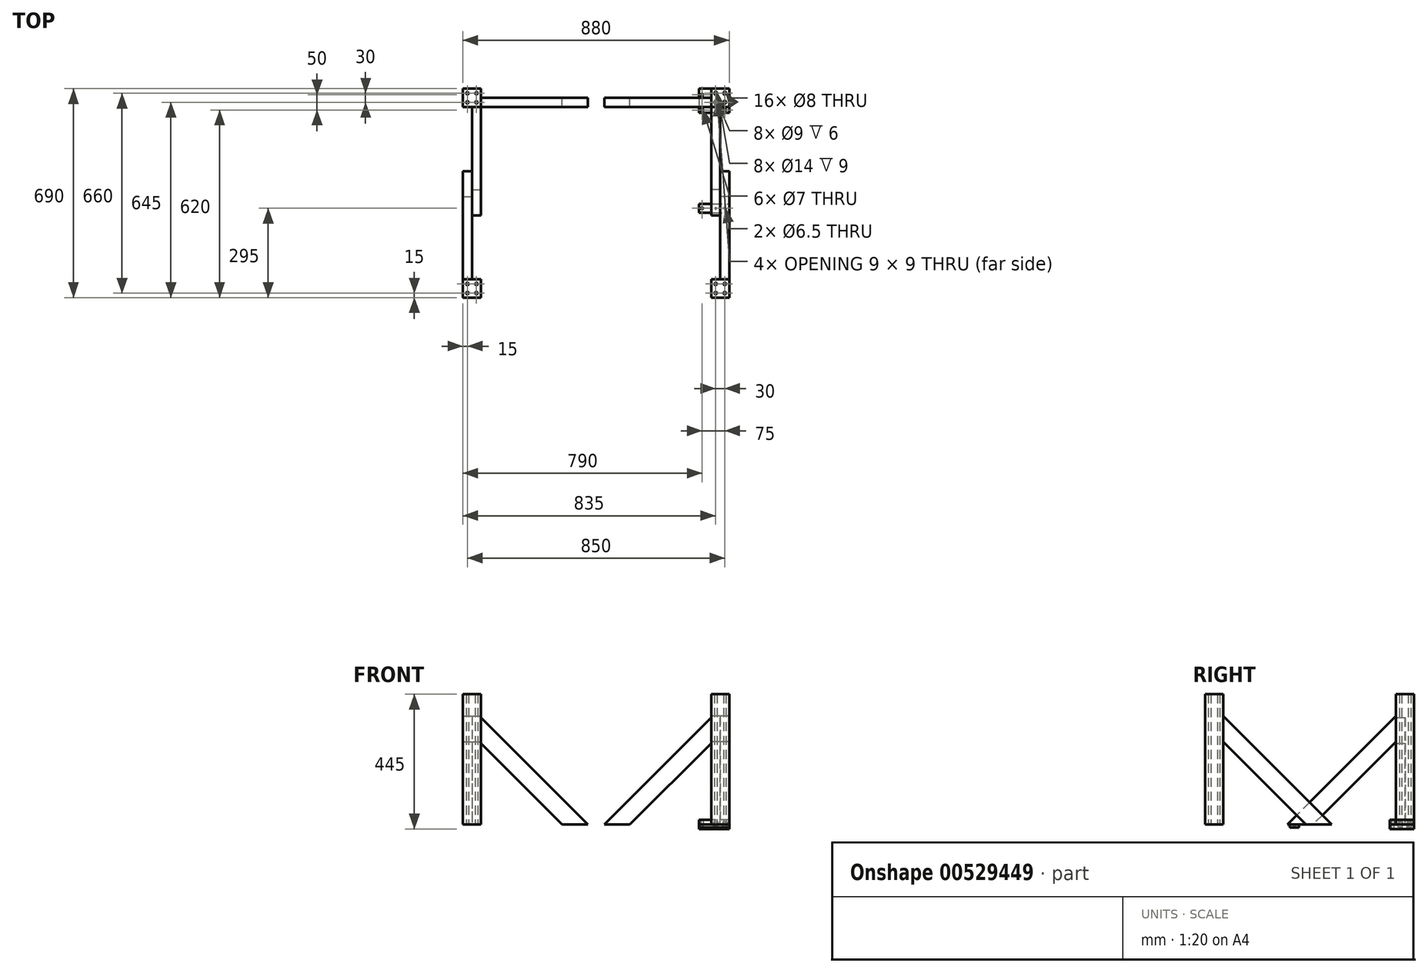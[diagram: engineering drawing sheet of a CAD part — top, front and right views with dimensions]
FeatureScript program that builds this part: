
annotation { "Feature Type Name" : "Feature", "Feature Type Description" : "" }
export const myFeature = defineFeature(function(context is Context, id is Id, definition is map)
    precondition{}
    {
        {
            var Q0;
            Q0=qCreatedBy(makeId("Top.planeOp"),FACE);
            var sketch = newSketch(context, id + "F0", { "sketchPlane" : qUnion([Q0])});
            skCircle(sketch, "E0", {"center": v(0, 0) * mm, "radius": 3 * mm, "construction": true});
            skCircle(sketch, "E1.0.1.0", {"center": v(0, 25) * mm, "radius": 3 * mm, "construction": true});
            skCircle(sketch, "E1.0.2.0", {"center": v(0, 50) * mm, "radius": 3 * mm, "construction": true});
            skCircle(sketch, "E1.0.3.0", {"center": v(0, 75) * mm, "radius": 3 * mm, "construction": true});
            skCircle(sketch, "E1.0.4.0", {"center": v(0, 100) * mm, "radius": 3 * mm, "construction": true});
            skCircle(sketch, "E1.1.0.0", {"center": v(25, 0) * mm, "radius": 3 * mm, "construction": true});
            skCircle(sketch, "E1.1.1.0", {"center": v(25, 25) * mm, "radius": 3 * mm, "construction": true});
            skCircle(sketch, "E1.1.2.0", {"center": v(25, 50) * mm, "radius": 3 * mm, "construction": true});
            skCircle(sketch, "E1.1.3.0", {"center": v(25, 75) * mm, "radius": 3 * mm, "construction": true});
            skCircle(sketch, "E1.1.4.0", {"center": v(25, 100) * mm, "radius": 3 * mm, "construction": true});
            skCircle(sketch, "E1.2.0.0", {"center": v(50, 0) * mm, "radius": 3 * mm, "construction": true});
            skCircle(sketch, "E1.2.1.0", {"center": v(50, 25) * mm, "radius": 3 * mm, "construction": true});
            skCircle(sketch, "E1.2.2.0", {"center": v(50, 50) * mm, "radius": 3 * mm, "construction": true});
            skCircle(sketch, "E1.2.3.0", {"center": v(50, 75) * mm, "radius": 3 * mm, "construction": true});
            skCircle(sketch, "E1.2.4.0", {"center": v(50, 100) * mm, "radius": 3 * mm, "construction": true});
            skCircle(sketch, "E1.3.0.0", {"center": v(75, 0) * mm, "radius": 3 * mm, "construction": true});
            skCircle(sketch, "E1.3.1.0", {"center": v(75, 25) * mm, "radius": 3 * mm, "construction": true});
            skCircle(sketch, "E1.3.2.0", {"center": v(75, 50) * mm, "radius": 3 * mm, "construction": true});
            skCircle(sketch, "E1.3.3.0", {"center": v(75, 75) * mm, "radius": 3 * mm, "construction": true});
            skCircle(sketch, "E1.3.4.0", {"center": v(75, 100) * mm, "radius": 3 * mm, "construction": true});
            skCircle(sketch, "E1.4.0.0", {"center": v(100, 0) * mm, "radius": 3 * mm, "construction": true});
            skCircle(sketch, "E1.4.1.0", {"center": v(100, 25) * mm, "radius": 3 * mm, "construction": true});
            skCircle(sketch, "E1.4.2.0", {"center": v(100, 50) * mm, "radius": 3 * mm, "construction": true});
            skCircle(sketch, "E1.4.3.0", {"center": v(100, 75) * mm, "radius": 3 * mm, "construction": true});
            skCircle(sketch, "E1.4.4.0", {"center": v(100, 100) * mm, "radius": 3 * mm, "construction": true});
            skLineSegment(sketch, "E1.direction1", {"start": v(0, 0) * mm, "end": v(25, 0) * mm, "construction": true});
            skLineSegment(sketch, "E1.direction2", {"start": v(0, 0) * mm, "end": v(0, 25) * mm, "construction": true});
            skCircle(sketch, "E2.0.1.0", {"center": v(0, -25) * mm, "radius": 3 * mm, "construction": true});
            skCircle(sketch, "E2.0.2.0", {"center": v(0, -50) * mm, "radius": 3 * mm, "construction": true});
            skCircle(sketch, "E2.0.3.0", {"center": v(0, -75) * mm, "radius": 3 * mm, "construction": true});
            skCircle(sketch, "E2.0.4.0", {"center": v(0, -100) * mm, "radius": 3 * mm, "construction": true});
            skCircle(sketch, "E2.0.5.0", {"center": v(0, -125) * mm, "radius": 3 * mm, "construction": true});
            skCircle(sketch, "E2.0.6.0", {"center": v(0, -150) * mm, "radius": 3 * mm, "construction": true});
            skCircle(sketch, "E2.0.7.0", {"center": v(0, -175) * mm, "radius": 3 * mm, "construction": true});
            skCircle(sketch, "E2.0.8.0", {"center": v(0, -200) * mm, "radius": 3 * mm, "construction": true});
            skCircle(sketch, "E2.0.9.0", {"center": v(0, -225) * mm, "radius": 3 * mm, "construction": true});
            skCircle(sketch, "E2.0.10.0", {"center": v(0, -250) * mm, "radius": 3 * mm, "construction": true});
            skCircle(sketch, "E2.0.11.0", {"center": v(0, -275) * mm, "radius": 3 * mm, "construction": true});
            skCircle(sketch, "E2.0.12.0", {"center": v(0, -300) * mm, "radius": 3 * mm, "construction": true});
            skCircle(sketch, "E2.0.13.0", {"center": v(0, -325) * mm, "radius": 3 * mm, "construction": true});
            skCircle(sketch, "E2.0.14.0", {"center": v(0, -350) * mm, "radius": 3 * mm, "construction": true});
            skCircle(sketch, "E2.0.15.0", {"center": v(0, -375) * mm, "radius": 3 * mm, "construction": true});
            skCircle(sketch, "E2.0.16.0", {"center": v(0, -400) * mm, "radius": 3 * mm, "construction": true});
            skCircle(sketch, "E2.0.17.0", {"center": v(0, -425) * mm, "radius": 3 * mm, "construction": true});
            skCircle(sketch, "E2.0.18.0", {"center": v(0, -450) * mm, "radius": 3 * mm, "construction": true});
            skCircle(sketch, "E2.0.19.0", {"center": v(0, -475) * mm, "radius": 3 * mm, "construction": true});
            skCircle(sketch, "E2.1.1.0", {"center": v(25, -25) * mm, "radius": 3 * mm, "construction": true});
            skCircle(sketch, "E2.1.2.0", {"center": v(25, -50) * mm, "radius": 3 * mm, "construction": true});
            skCircle(sketch, "E2.1.3.0", {"center": v(25, -75) * mm, "radius": 3 * mm, "construction": true});
            skCircle(sketch, "E2.1.4.0", {"center": v(25, -100) * mm, "radius": 3 * mm, "construction": true});
            skCircle(sketch, "E2.1.5.0", {"center": v(25, -125) * mm, "radius": 3 * mm, "construction": true});
            skCircle(sketch, "E2.1.6.0", {"center": v(25, -150) * mm, "radius": 3 * mm, "construction": true});
            skCircle(sketch, "E2.1.7.0", {"center": v(25, -175) * mm, "radius": 3 * mm, "construction": true});
            skCircle(sketch, "E2.1.8.0", {"center": v(25, -200) * mm, "radius": 3 * mm, "construction": true});
            skCircle(sketch, "E2.1.9.0", {"center": v(25, -225) * mm, "radius": 3 * mm, "construction": true});
            skCircle(sketch, "E2.1.10.0", {"center": v(25, -250) * mm, "radius": 3 * mm, "construction": true});
            skCircle(sketch, "E2.1.11.0", {"center": v(25, -275) * mm, "radius": 3 * mm, "construction": true});
            skCircle(sketch, "E2.1.12.0", {"center": v(25, -300) * mm, "radius": 3 * mm, "construction": true});
            skCircle(sketch, "E2.1.13.0", {"center": v(25, -325) * mm, "radius": 3 * mm, "construction": true});
            skCircle(sketch, "E2.1.14.0", {"center": v(25, -350) * mm, "radius": 3 * mm, "construction": true});
            skCircle(sketch, "E2.1.15.0", {"center": v(25, -375) * mm, "radius": 3 * mm, "construction": true});
            skCircle(sketch, "E2.1.16.0", {"center": v(25, -400) * mm, "radius": 3 * mm, "construction": true});
            skCircle(sketch, "E2.1.17.0", {"center": v(25, -425) * mm, "radius": 3 * mm, "construction": true});
            skCircle(sketch, "E2.1.18.0", {"center": v(25, -450) * mm, "radius": 3 * mm, "construction": true});
            skCircle(sketch, "E2.1.19.0", {"center": v(25, -475) * mm, "radius": 3 * mm, "construction": true});
            skCircle(sketch, "E2.2.1.0", {"center": v(50, -25) * mm, "radius": 3 * mm, "construction": true});
            skCircle(sketch, "E2.2.2.0", {"center": v(50, -50) * mm, "radius": 3 * mm, "construction": true});
            skCircle(sketch, "E2.2.3.0", {"center": v(50, -75) * mm, "radius": 3 * mm, "construction": true});
            skCircle(sketch, "E2.2.4.0", {"center": v(50, -100) * mm, "radius": 3 * mm, "construction": true});
            skCircle(sketch, "E2.2.5.0", {"center": v(50, -125) * mm, "radius": 3 * mm, "construction": true});
            skCircle(sketch, "E2.2.6.0", {"center": v(50, -150) * mm, "radius": 3 * mm, "construction": true});
            skCircle(sketch, "E2.2.7.0", {"center": v(50, -175) * mm, "radius": 3 * mm, "construction": true});
            skCircle(sketch, "E2.2.8.0", {"center": v(50, -200) * mm, "radius": 3 * mm, "construction": true});
            skCircle(sketch, "E2.2.9.0", {"center": v(50, -225) * mm, "radius": 3 * mm, "construction": true});
            skCircle(sketch, "E2.2.10.0", {"center": v(50, -250) * mm, "radius": 3 * mm, "construction": true});
            skCircle(sketch, "E2.2.11.0", {"center": v(50, -275) * mm, "radius": 3 * mm, "construction": true});
            skCircle(sketch, "E2.2.12.0", {"center": v(50, -300) * mm, "radius": 3 * mm, "construction": true});
            skCircle(sketch, "E2.2.13.0", {"center": v(50, -325) * mm, "radius": 3 * mm, "construction": true});
            skCircle(sketch, "E2.2.14.0", {"center": v(50, -350) * mm, "radius": 3 * mm, "construction": true});
            skCircle(sketch, "E2.2.15.0", {"center": v(50, -375) * mm, "radius": 3 * mm, "construction": true});
            skCircle(sketch, "E2.2.16.0", {"center": v(50, -400) * mm, "radius": 3 * mm, "construction": true});
            skCircle(sketch, "E2.2.17.0", {"center": v(50, -425) * mm, "radius": 3 * mm, "construction": true});
            skCircle(sketch, "E2.2.18.0", {"center": v(50, -450) * mm, "radius": 3 * mm, "construction": true});
            skCircle(sketch, "E2.2.19.0", {"center": v(50, -475) * mm, "radius": 3 * mm, "construction": true});
            skCircle(sketch, "E2.3.1.0", {"center": v(75, -25) * mm, "radius": 3 * mm, "construction": true});
            skCircle(sketch, "E2.3.2.0", {"center": v(75, -50) * mm, "radius": 3 * mm, "construction": true});
            skCircle(sketch, "E2.3.3.0", {"center": v(75, -75) * mm, "radius": 3 * mm, "construction": true});
            skCircle(sketch, "E2.3.4.0", {"center": v(75, -100) * mm, "radius": 3 * mm, "construction": true});
            skCircle(sketch, "E2.3.5.0", {"center": v(75, -125) * mm, "radius": 3 * mm, "construction": true});
            skCircle(sketch, "E2.3.6.0", {"center": v(75, -150) * mm, "radius": 3 * mm, "construction": true});
            skCircle(sketch, "E2.3.7.0", {"center": v(75, -175) * mm, "radius": 3 * mm, "construction": true});
            skCircle(sketch, "E2.3.8.0", {"center": v(75, -200) * mm, "radius": 3 * mm, "construction": true});
            skCircle(sketch, "E2.3.9.0", {"center": v(75, -225) * mm, "radius": 3 * mm, "construction": true});
            skCircle(sketch, "E2.3.10.0", {"center": v(75, -250) * mm, "radius": 3 * mm, "construction": true});
            skCircle(sketch, "E2.3.11.0", {"center": v(75, -275) * mm, "radius": 3 * mm, "construction": true});
            skCircle(sketch, "E2.3.12.0", {"center": v(75, -300) * mm, "radius": 3 * mm, "construction": true});
            skCircle(sketch, "E2.3.13.0", {"center": v(75, -325) * mm, "radius": 3 * mm, "construction": true});
            skCircle(sketch, "E2.3.14.0", {"center": v(75, -350) * mm, "radius": 3 * mm, "construction": true});
            skCircle(sketch, "E2.3.15.0", {"center": v(75, -375) * mm, "radius": 3 * mm, "construction": true});
            skCircle(sketch, "E2.3.16.0", {"center": v(75, -400) * mm, "radius": 3 * mm, "construction": true});
            skCircle(sketch, "E2.3.17.0", {"center": v(75, -425) * mm, "radius": 3 * mm, "construction": true});
            skCircle(sketch, "E2.3.18.0", {"center": v(75, -450) * mm, "radius": 3 * mm, "construction": true});
            skCircle(sketch, "E2.3.19.0", {"center": v(75, -475) * mm, "radius": 3 * mm, "construction": true});
            skCircle(sketch, "E2.4.1.0", {"center": v(100, -25) * mm, "radius": 3 * mm, "construction": true});
            skCircle(sketch, "E2.4.2.0", {"center": v(100, -50) * mm, "radius": 3 * mm, "construction": true});
            skCircle(sketch, "E2.4.3.0", {"center": v(100, -75) * mm, "radius": 3 * mm, "construction": true});
            skCircle(sketch, "E2.4.4.0", {"center": v(100, -100) * mm, "radius": 3 * mm, "construction": true});
            skCircle(sketch, "E2.4.5.0", {"center": v(100, -125) * mm, "radius": 3 * mm, "construction": true});
            skCircle(sketch, "E2.4.6.0", {"center": v(100, -150) * mm, "radius": 3 * mm, "construction": true});
            skCircle(sketch, "E2.4.7.0", {"center": v(100, -175) * mm, "radius": 3 * mm, "construction": true});
            skCircle(sketch, "E2.4.8.0", {"center": v(100, -200) * mm, "radius": 3 * mm, "construction": true});
            skCircle(sketch, "E2.4.9.0", {"center": v(100, -225) * mm, "radius": 3 * mm, "construction": true});
            skCircle(sketch, "E2.4.10.0", {"center": v(100, -250) * mm, "radius": 3 * mm, "construction": true});
            skCircle(sketch, "E2.4.11.0", {"center": v(100, -275) * mm, "radius": 3 * mm, "construction": true});
            skCircle(sketch, "E2.4.12.0", {"center": v(100, -300) * mm, "radius": 3 * mm, "construction": true});
            skCircle(sketch, "E2.4.13.0", {"center": v(100, -325) * mm, "radius": 3 * mm, "construction": true});
            skCircle(sketch, "E2.4.14.0", {"center": v(100, -350) * mm, "radius": 3 * mm, "construction": true});
            skCircle(sketch, "E2.4.15.0", {"center": v(100, -375) * mm, "radius": 3 * mm, "construction": true});
            skCircle(sketch, "E2.4.16.0", {"center": v(100, -400) * mm, "radius": 3 * mm, "construction": true});
            skCircle(sketch, "E2.4.17.0", {"center": v(100, -425) * mm, "radius": 3 * mm, "construction": true});
            skCircle(sketch, "E2.4.18.0", {"center": v(100, -450) * mm, "radius": 3 * mm, "construction": true});
            skCircle(sketch, "E2.4.19.0", {"center": v(100, -475) * mm, "radius": 3 * mm, "construction": true});
            skLineSegment(sketch, "E2.direction2", {"start": v(0, 0) * mm, "end": v(0, -25) * mm, "construction": true});
            skCircle(sketch, "E3.1.0.0", {"center": v(-25, 0) * mm, "radius": 3 * mm, "construction": true});
            skCircle(sketch, "E3.1.1.0", {"center": v(-25, 25) * mm, "radius": 3 * mm, "construction": true});
            skCircle(sketch, "E3.1.2.0", {"center": v(-25, 50) * mm, "radius": 3 * mm, "construction": true});
            skCircle(sketch, "E3.1.3.0", {"center": v(-25, 75) * mm, "radius": 3 * mm, "construction": true});
            skCircle(sketch, "E3.1.4.0", {"center": v(-25, 100) * mm, "radius": 3 * mm, "construction": true});
            skCircle(sketch, "E3.2.0.0", {"center": v(-50, 0) * mm, "radius": 3 * mm, "construction": true});
            skCircle(sketch, "E3.2.1.0", {"center": v(-50, 25) * mm, "radius": 3 * mm, "construction": true});
            skCircle(sketch, "E3.2.2.0", {"center": v(-50, 50) * mm, "radius": 3 * mm, "construction": true});
            skCircle(sketch, "E3.2.3.0", {"center": v(-50, 75) * mm, "radius": 3 * mm, "construction": true});
            skCircle(sketch, "E3.2.4.0", {"center": v(-50, 100) * mm, "radius": 3 * mm, "construction": true});
            skLineSegment(sketch, "E3.direction1", {"start": v(0, 0) * mm, "end": v(-25, 0) * mm, "construction": true});
            skCircle(sketch, "E4.0.3.0", {"center": v(-75, 0) * mm, "radius": 3 * mm, "construction": true});
            skCircle(sketch, "E4.0.3.1", {"center": v(-75, 25) * mm, "radius": 3 * mm, "construction": true});
            skCircle(sketch, "E4.0.3.2", {"center": v(-75, 50) * mm, "radius": 3 * mm, "construction": true});
            skCircle(sketch, "E4.0.3.3", {"center": v(-75, 75) * mm, "radius": 3 * mm, "construction": true});
            skCircle(sketch, "E4.0.3.4", {"center": v(-75, 100) * mm, "radius": 3 * mm, "construction": true});
            skCircle(sketch, "E4.0.4.0", {"center": v(-100, 0) * mm, "radius": 3 * mm, "construction": true});
            skCircle(sketch, "E4.0.4.1", {"center": v(-100, 25) * mm, "radius": 3 * mm, "construction": true});
            skCircle(sketch, "E4.0.4.2", {"center": v(-100, 50) * mm, "radius": 3 * mm, "construction": true});
            skCircle(sketch, "E4.0.4.3", {"center": v(-100, 75) * mm, "radius": 3 * mm, "construction": true});
            skCircle(sketch, "E4.0.4.4", {"center": v(-100, 100) * mm, "radius": 3 * mm, "construction": true});
            skCircle(sketch, "E4.0.5.0", {"center": v(-125, 0) * mm, "radius": 3 * mm, "construction": true});
            skCircle(sketch, "E4.0.5.1", {"center": v(-125, 25) * mm, "radius": 3 * mm, "construction": true});
            skCircle(sketch, "E4.0.5.2", {"center": v(-125, 50) * mm, "radius": 3 * mm, "construction": true});
            skCircle(sketch, "E4.0.5.3", {"center": v(-125, 75) * mm, "radius": 3 * mm, "construction": true});
            skCircle(sketch, "E4.0.5.4", {"center": v(-125, 100) * mm, "radius": 3 * mm, "construction": true});
            skCircle(sketch, "E4.0.6.0", {"center": v(-150, 0) * mm, "radius": 3 * mm, "construction": true});
            skCircle(sketch, "E4.0.6.1", {"center": v(-150, 25) * mm, "radius": 3 * mm, "construction": true});
            skCircle(sketch, "E4.0.6.2", {"center": v(-150, 50) * mm, "radius": 3 * mm, "construction": true});
            skCircle(sketch, "E4.0.6.3", {"center": v(-150, 75) * mm, "radius": 3 * mm, "construction": true});
            skCircle(sketch, "E4.0.6.4", {"center": v(-150, 100) * mm, "radius": 3 * mm, "construction": true});
            skCircle(sketch, "E4.0.7.0", {"center": v(-175, 0) * mm, "radius": 3 * mm, "construction": true});
            skCircle(sketch, "E4.0.7.1", {"center": v(-175, 25) * mm, "radius": 3 * mm, "construction": true});
            skCircle(sketch, "E4.0.7.2", {"center": v(-175, 50) * mm, "radius": 3 * mm, "construction": true});
            skCircle(sketch, "E4.0.7.3", {"center": v(-175, 75) * mm, "radius": 3 * mm, "construction": true});
            skCircle(sketch, "E4.0.7.4", {"center": v(-175, 100) * mm, "radius": 3 * mm, "construction": true});
            skCircle(sketch, "E4.0.8.0", {"center": v(-200, 0) * mm, "radius": 3 * mm, "construction": true});
            skCircle(sketch, "E4.0.8.1", {"center": v(-200, 25) * mm, "radius": 3 * mm, "construction": true});
            skCircle(sketch, "E4.0.8.2", {"center": v(-200, 50) * mm, "radius": 3 * mm, "construction": true});
            skCircle(sketch, "E4.0.8.3", {"center": v(-200, 75) * mm, "radius": 3 * mm, "construction": true});
            skCircle(sketch, "E4.0.8.4", {"center": v(-200, 100) * mm, "radius": 3 * mm, "construction": true});
            skCircle(sketch, "E4.0.9.0", {"center": v(-225, 0) * mm, "radius": 3 * mm, "construction": true});
            skCircle(sketch, "E4.0.9.1", {"center": v(-225, 25) * mm, "radius": 3 * mm, "construction": true});
            skCircle(sketch, "E4.0.9.2", {"center": v(-225, 50) * mm, "radius": 3 * mm, "construction": true});
            skCircle(sketch, "E4.0.9.3", {"center": v(-225, 75) * mm, "radius": 3 * mm, "construction": true});
            skCircle(sketch, "E4.0.9.4", {"center": v(-225, 100) * mm, "radius": 3 * mm, "construction": true});
            skCircle(sketch, "E4.0.10.0", {"center": v(-250, 0) * mm, "radius": 3 * mm, "construction": true});
            skCircle(sketch, "E4.0.10.1", {"center": v(-250, 25) * mm, "radius": 3 * mm, "construction": true});
            skCircle(sketch, "E4.0.10.2", {"center": v(-250, 50) * mm, "radius": 3 * mm, "construction": true});
            skCircle(sketch, "E4.0.10.3", {"center": v(-250, 75) * mm, "radius": 3 * mm, "construction": true});
            skCircle(sketch, "E4.0.10.4", {"center": v(-250, 100) * mm, "radius": 3 * mm, "construction": true});
            skCircle(sketch, "E4.0.11.0", {"center": v(-275, 0) * mm, "radius": 3 * mm, "construction": true});
            skCircle(sketch, "E4.0.11.1", {"center": v(-275, 25) * mm, "radius": 3 * mm, "construction": true});
            skCircle(sketch, "E4.0.11.2", {"center": v(-275, 50) * mm, "radius": 3 * mm, "construction": true});
            skCircle(sketch, "E4.0.11.3", {"center": v(-275, 75) * mm, "radius": 3 * mm, "construction": true});
            skCircle(sketch, "E4.0.11.4", {"center": v(-275, 100) * mm, "radius": 3 * mm, "construction": true});
            skCircle(sketch, "E4.0.12.0", {"center": v(-300, 0) * mm, "radius": 3 * mm, "construction": true});
            skCircle(sketch, "E4.0.12.1", {"center": v(-300, 25) * mm, "radius": 3 * mm, "construction": true});
            skCircle(sketch, "E4.0.12.2", {"center": v(-300, 50) * mm, "radius": 3 * mm, "construction": true});
            skCircle(sketch, "E4.0.12.3", {"center": v(-300, 75) * mm, "radius": 3 * mm, "construction": true});
            skCircle(sketch, "E4.0.12.4", {"center": v(-300, 100) * mm, "radius": 3 * mm, "construction": true});
            skCircle(sketch, "E4.0.13.0", {"center": v(-325, 0) * mm, "radius": 3 * mm, "construction": true});
            skCircle(sketch, "E4.0.13.1", {"center": v(-325, 25) * mm, "radius": 3 * mm, "construction": true});
            skCircle(sketch, "E4.0.13.2", {"center": v(-325, 50) * mm, "radius": 3 * mm, "construction": true});
            skCircle(sketch, "E4.0.13.3", {"center": v(-325, 75) * mm, "radius": 3 * mm, "construction": true});
            skCircle(sketch, "E4.0.13.4", {"center": v(-325, 100) * mm, "radius": 3 * mm, "construction": true});
            skCircle(sketch, "E4.0.14.0", {"center": v(-350, 0) * mm, "radius": 3 * mm, "construction": true});
            skCircle(sketch, "E4.0.14.1", {"center": v(-350, 25) * mm, "radius": 3 * mm, "construction": true});
            skCircle(sketch, "E4.0.14.2", {"center": v(-350, 50) * mm, "radius": 3 * mm, "construction": true});
            skCircle(sketch, "E4.0.14.3", {"center": v(-350, 75) * mm, "radius": 3 * mm, "construction": true});
            skCircle(sketch, "E4.0.14.4", {"center": v(-350, 100) * mm, "radius": 3 * mm, "construction": true});
            skCircle(sketch, "E4.0.15.0", {"center": v(-375, 0) * mm, "radius": 3 * mm, "construction": true});
            skCircle(sketch, "E4.0.15.1", {"center": v(-375, 25) * mm, "radius": 3 * mm, "construction": true});
            skCircle(sketch, "E4.0.15.2", {"center": v(-375, 50) * mm, "radius": 3 * mm, "construction": true});
            skCircle(sketch, "E4.0.15.3", {"center": v(-375, 75) * mm, "radius": 3 * mm, "construction": true});
            skCircle(sketch, "E4.0.15.4", {"center": v(-375, 100) * mm, "radius": 3 * mm, "construction": true});
            skCircle(sketch, "E4.0.16.0", {"center": v(-400, 0) * mm, "radius": 3 * mm, "construction": true});
            skCircle(sketch, "E4.0.16.1", {"center": v(-400, 25) * mm, "radius": 3 * mm, "construction": true});
            skCircle(sketch, "E4.0.16.2", {"center": v(-400, 50) * mm, "radius": 3 * mm, "construction": true});
            skCircle(sketch, "E4.0.16.3", {"center": v(-400, 75) * mm, "radius": 3 * mm, "construction": true});
            skCircle(sketch, "E4.0.16.4", {"center": v(-400, 100) * mm, "radius": 3 * mm, "construction": true});
            skCircle(sketch, "E4.0.17.0", {"center": v(-425, 0) * mm, "radius": 3 * mm, "construction": true});
            skCircle(sketch, "E4.0.17.1", {"center": v(-425, 25) * mm, "radius": 3 * mm, "construction": true});
            skCircle(sketch, "E4.0.17.2", {"center": v(-425, 50) * mm, "radius": 3 * mm, "construction": true});
            skCircle(sketch, "E4.0.17.3", {"center": v(-425, 75) * mm, "radius": 3 * mm, "construction": true});
            skCircle(sketch, "E4.0.17.4", {"center": v(-425, 100) * mm, "radius": 3 * mm, "construction": true});
            skCircle(sketch, "E4.0.18.0", {"center": v(-450, 0) * mm, "radius": 3 * mm, "construction": true});
            skCircle(sketch, "E4.0.18.1", {"center": v(-450, 25) * mm, "radius": 3 * mm, "construction": true});
            skCircle(sketch, "E4.0.18.2", {"center": v(-450, 50) * mm, "radius": 3 * mm, "construction": true});
            skCircle(sketch, "E4.0.18.3", {"center": v(-450, 75) * mm, "radius": 3 * mm, "construction": true});
            skCircle(sketch, "E4.0.18.4", {"center": v(-450, 100) * mm, "radius": 3 * mm, "construction": true});
            skCircle(sketch, "E4.0.19.0", {"center": v(-475, 0) * mm, "radius": 3 * mm, "construction": true});
            skCircle(sketch, "E4.0.19.1", {"center": v(-475, 25) * mm, "radius": 3 * mm, "construction": true});
            skCircle(sketch, "E4.0.19.2", {"center": v(-475, 50) * mm, "radius": 3 * mm, "construction": true});
            skCircle(sketch, "E4.0.19.3", {"center": v(-475, 75) * mm, "radius": 3 * mm, "construction": true});
            skCircle(sketch, "E4.0.19.4", {"center": v(-475, 100) * mm, "radius": 3 * mm, "construction": true});
            skCircle(sketch, "E4.0.20.0", {"center": v(-500, 0) * mm, "radius": 3 * mm, "construction": true});
            skCircle(sketch, "E4.0.20.1", {"center": v(-500, 25) * mm, "radius": 3 * mm, "construction": true});
            skCircle(sketch, "E4.0.20.2", {"center": v(-500, 50) * mm, "radius": 3 * mm, "construction": true});
            skCircle(sketch, "E4.0.20.3", {"center": v(-500, 75) * mm, "radius": 3 * mm, "construction": true});
            skCircle(sketch, "E4.0.20.4", {"center": v(-500, 100) * mm, "radius": 3 * mm, "construction": true});
            skCircle(sketch, "E4.0.21.0", {"center": v(-525, 0) * mm, "radius": 3 * mm, "construction": true});
            skCircle(sketch, "E4.0.21.1", {"center": v(-525, 25) * mm, "radius": 3 * mm, "construction": true});
            skCircle(sketch, "E4.0.21.2", {"center": v(-525, 50) * mm, "radius": 3 * mm, "construction": true});
            skCircle(sketch, "E4.0.21.3", {"center": v(-525, 75) * mm, "radius": 3 * mm, "construction": true});
            skCircle(sketch, "E4.0.21.4", {"center": v(-525, 100) * mm, "radius": 3 * mm, "construction": true});
            skCircle(sketch, "E4.0.22.0", {"center": v(-550, 0) * mm, "radius": 3 * mm, "construction": true});
            skCircle(sketch, "E4.0.22.1", {"center": v(-550, 25) * mm, "radius": 3 * mm, "construction": true});
            skCircle(sketch, "E4.0.22.2", {"center": v(-550, 50) * mm, "radius": 3 * mm, "construction": true});
            skCircle(sketch, "E4.0.22.3", {"center": v(-550, 75) * mm, "radius": 3 * mm, "construction": true});
            skCircle(sketch, "E4.0.22.4", {"center": v(-550, 100) * mm, "radius": 3 * mm, "construction": true});
            skCircle(sketch, "E4.0.23.0", {"center": v(-575, 0) * mm, "radius": 3 * mm, "construction": true});
            skCircle(sketch, "E4.0.23.1", {"center": v(-575, 25) * mm, "radius": 3 * mm, "construction": true});
            skCircle(sketch, "E4.0.23.2", {"center": v(-575, 50) * mm, "radius": 3 * mm, "construction": true});
            skCircle(sketch, "E4.0.23.3", {"center": v(-575, 75) * mm, "radius": 3 * mm, "construction": true});
            skCircle(sketch, "E4.0.23.4", {"center": v(-575, 100) * mm, "radius": 3 * mm, "construction": true});
            skCircle(sketch, "E4.0.24.0", {"center": v(-600, 0) * mm, "radius": 3 * mm, "construction": true});
            skCircle(sketch, "E4.0.24.1", {"center": v(-600, 25) * mm, "radius": 3 * mm, "construction": true});
            skCircle(sketch, "E4.0.24.2", {"center": v(-600, 50) * mm, "radius": 3 * mm, "construction": true});
            skCircle(sketch, "E4.0.24.3", {"center": v(-600, 75) * mm, "radius": 3 * mm, "construction": true});
            skCircle(sketch, "E4.0.24.4", {"center": v(-600, 100) * mm, "radius": 3 * mm, "construction": true});
            skCircle(sketch, "E5.0.25.0", {"center": v(-625, 0) * mm, "radius": 3 * mm, "construction": true});
            skCircle(sketch, "E5.0.25.1", {"center": v(-625, 25) * mm, "radius": 3 * mm, "construction": true});
            skCircle(sketch, "E5.0.25.2", {"center": v(-625, 50) * mm, "radius": 3 * mm, "construction": true});
            skCircle(sketch, "E5.0.25.3", {"center": v(-625, 75) * mm, "radius": 3 * mm, "construction": true});
            skCircle(sketch, "E5.0.25.4", {"center": v(-625, 100) * mm, "radius": 3 * mm, "construction": true});
            skCircle(sketch, "E5.0.26.0", {"center": v(-650, 0) * mm, "radius": 3 * mm, "construction": true});
            skCircle(sketch, "E5.0.26.1", {"center": v(-650, 25) * mm, "radius": 3 * mm, "construction": true});
            skCircle(sketch, "E5.0.26.2", {"center": v(-650, 50) * mm, "radius": 3 * mm, "construction": true});
            skCircle(sketch, "E5.0.26.3", {"center": v(-650, 75) * mm, "radius": 3 * mm, "construction": true});
            skCircle(sketch, "E5.0.26.4", {"center": v(-650, 100) * mm, "radius": 3 * mm, "construction": true});
            skCircle(sketch, "E5.0.27.0", {"center": v(-675, 0) * mm, "radius": 3 * mm, "construction": true});
            skCircle(sketch, "E5.0.27.1", {"center": v(-675, 25) * mm, "radius": 3 * mm, "construction": true});
            skCircle(sketch, "E5.0.27.2", {"center": v(-675, 50) * mm, "radius": 3 * mm, "construction": true});
            skCircle(sketch, "E5.0.27.3", {"center": v(-675, 75) * mm, "radius": 3 * mm, "construction": true});
            skCircle(sketch, "E5.0.27.4", {"center": v(-675, 100) * mm, "radius": 3 * mm, "construction": true});
            skCircle(sketch, "E5.0.28.0", {"center": v(-700, 0) * mm, "radius": 3 * mm, "construction": true});
            skCircle(sketch, "E5.0.28.1", {"center": v(-700, 25) * mm, "radius": 3 * mm, "construction": true});
            skCircle(sketch, "E5.0.28.2", {"center": v(-700, 50) * mm, "radius": 3 * mm, "construction": true});
            skCircle(sketch, "E5.0.28.3", {"center": v(-700, 75) * mm, "radius": 3 * mm, "construction": true});
            skCircle(sketch, "E5.0.28.4", {"center": v(-700, 100) * mm, "radius": 3 * mm, "construction": true});
            skCircle(sketch, "E5.0.29.0", {"center": v(-725, 0) * mm, "radius": 3 * mm, "construction": true});
            skCircle(sketch, "E5.0.29.1", {"center": v(-725, 25) * mm, "radius": 3 * mm, "construction": true});
            skCircle(sketch, "E5.0.29.2", {"center": v(-725, 50) * mm, "radius": 3 * mm, "construction": true});
            skCircle(sketch, "E5.0.29.3", {"center": v(-725, 75) * mm, "radius": 3 * mm, "construction": true});
            skCircle(sketch, "E5.0.29.4", {"center": v(-725, 100) * mm, "radius": 3 * mm, "construction": true});
            skSolve(sketch);
        }
        {
            var Q0;
            Q0=qCreatedBy(makeId("Top.planeOp"),FACE);
            var sketch = newSketch(context, id + "F1", { "sketchPlane" : qUnion([Q0])});
            skLineSegment(sketch, "E6.bottom", {"start": v(30, 35) * mm, "end": v(90, 35) * mm});
            skLineSegment(sketch, "E6.top", {"start": v(30, 95) * mm, "end": v(90, 95) * mm});
            skLineSegment(sketch, "E6.left", {"start": v(30, 35) * mm, "end": v(30, 95) * mm});
            skLineSegment(sketch, "E6.right", {"start": v(90, 35) * mm, "end": v(90, 95) * mm});
            skCircle(sketch, "E7", {"center": v(45, 80) * mm, "radius": 4 * mm});
            skCircle(sketch, "E8.0.1.0", {"center": v(45, 50) * mm, "radius": 4 * mm});
            skCircle(sketch, "E8.1.0.0", {"center": v(75, 80) * mm, "radius": 4 * mm});
            skCircle(sketch, "E8.1.1.0", {"center": v(75, 50) * mm, "radius": 4 * mm});
            skLineSegment(sketch, "E8.direction1", {"start": v(45, 80) * mm, "end": v(75, 80) * mm, "construction": true});
            skLineSegment(sketch, "E8.direction2", {"start": v(45, 80) * mm, "end": v(45, 50) * mm, "construction": true});
            skSolve(sketch);
        }
        {
            var Q0;
            Q0=qCreatedBy(makeId("Top.planeOp"),FACE);
            var sketch = newSketch(context, id + "F2", { "sketchPlane" : qUnion([Q0])});
            skPoint(sketch, "E9.0", {"position": v(90, 95) * mm});
            skLineSegment(sketch, "E10.bottom", {"start": v(90, 95) * mm, "end": v(-10, 95) * mm});
            skLineSegment(sketch, "E10.top", {"start": v(90, 15) * mm, "end": v(-10, 15) * mm});
            skLineSegment(sketch, "E10.left", {"start": v(90, 95) * mm, "end": v(90, 15) * mm});
            skLineSegment(sketch, "E10.right", {"start": v(-10, 95) * mm, "end": v(-10, 15) * mm});
            skPoint(sketch, "E11.0", {"position": v(0, 75) * mm});
            skPoint(sketch, "E11.1", {"position": v(0, 50) * mm});
            skPoint(sketch, "E11.2", {"position": v(0, 25) * mm});
            skPoint(sketch, "E11.3", {"position": v(25, 25) * mm});
            skPoint(sketch, "E11.4", {"position": v(50, 25) * mm});
            skPoint(sketch, "E11.5", {"position": v(75, 25) * mm});
            skCircle(sketch, "E12", {"center": v(0, 75) * mm, "radius": 3.5 * mm});
            skCircle(sketch, "E13", {"center": v(0, 25) * mm, "radius": 3.5 * mm});
            skCircle(sketch, "E14", {"center": v(75, 25) * mm, "radius": 3.5 * mm});
            skPoint(sketch, "E15.0", {"position": v(45, 80) * mm});
            skPoint(sketch, "E15.1", {"position": v(75, 80) * mm});
            skPoint(sketch, "E15.2", {"position": v(75, 50) * mm});
            skPoint(sketch, "E15.3", {"position": v(45, 50) * mm});
            skCircle(sketch, "E16", {"center": v(45, 80) * mm, "radius": 4.5 * mm});
            skCircle(sketch, "E17", {"center": v(45, 50) * mm, "radius": 4.5 * mm});
            skCircle(sketch, "E18", {"center": v(75, 80) * mm, "radius": 4.5 * mm});
            skCircle(sketch, "E19", {"center": v(75, 50) * mm, "radius": 4.5 * mm});
            skSolve(sketch);
        }
        {
            var Q0;
            Q0=makeQuery(id+"F2.imprint","IMPRINT",FACE,{"disambiguationData":[TD([[makeQuery(id+"F2.imprint","IMPRINT",EDGE,{"derivedFrom":sQuery(id+"F2.wireOp",EDGE,"E10.bottom")}),1.0]])]});
            extrude(context, id + "F3", {"entities" : qUnion([Q0]), "depth" : 15 * mm, "offsetDistance" : 25 * mm});
        }
        {
            var Q0;
            Q0=makeQuery(id+"F3.opExtrude","CAP_FACE",FACE,{"disambiguationData":[OSD([sQuery(id+"F2.wireOp",EDGE,"E10.bottom"),sQuery(id+"F2.wireOp",EDGE,"E10.top"),sQuery(id+"F2.wireOp",EDGE,"E10.left"),sQuery(id+"F2.wireOp",EDGE,"E10.right"),sQuery(id+"F2.wireOp",EDGE,"E12"),sQuery(id+"F2.wireOp",EDGE,"E13"),sQuery(id+"F2.wireOp",EDGE,"E14"),sQuery(id+"F2.wireOp",EDGE,"E16"),sQuery(id+"F2.wireOp",EDGE,"E17"),sQuery(id+"F2.wireOp",EDGE,"E18"),sQuery(id+"F2.wireOp",EDGE,"E19")])],"isStart":true});
            var sketch = newSketch(context, id + "F4", { "sketchPlane" : qUnion([Q0])});
            skPoint(sketch, "E20.0", {"position": v(45, -50) * mm});
            skPoint(sketch, "E20.1", {"position": v(75, -50) * mm});
            skPoint(sketch, "E20.2", {"position": v(75, -80) * mm});
            skPoint(sketch, "E20.3", {"position": v(45, -80) * mm});
            skCircle(sketch, "E21", {"center": v(45, -50) * mm, "radius": 7 * mm});
            skCircle(sketch, "E22", {"center": v(75, -50) * mm, "radius": 7 * mm});
            skCircle(sketch, "E23", {"center": v(75, -80) * mm, "radius": 7 * mm});
            skCircle(sketch, "E24", {"center": v(45, -80) * mm, "radius": 7 * mm});
            skSolve(sketch);
        }
        {
            var Q0;
            Q0 = qSketchRegion(id + "F4", true);
            extrude(context, id + "F5", {"entities" : qUnion([Q0]), "operationType" : NewBodyOperationType.REMOVE, "oppositeDirection" : true, "depth" : 9 * mm, "offsetDistance" : 25 * mm});
        }
        {
            var Q0;
            Q0=makeQuery(id+"F3.opExtrude","SWEPT_BODY",BODY,{"disambiguationData":[OSD([sQuery(id+"F2.wireOp",EDGE,"E10.bottom"),sQuery(id+"F2.wireOp",EDGE,"E10.top"),sQuery(id+"F2.wireOp",EDGE,"E10.left"),sQuery(id+"F2.wireOp",EDGE,"E10.right"),sQuery(id+"F2.wireOp",EDGE,"E12"),sQuery(id+"F2.wireOp",EDGE,"E13"),sQuery(id+"F2.wireOp",EDGE,"E14"),sQuery(id+"F2.wireOp",EDGE,"E16"),sQuery(id+"F2.wireOp",EDGE,"E17"),sQuery(id+"F2.wireOp",EDGE,"E18"),sQuery(id+"F2.wireOp",EDGE,"E19")])]});
            transform(context, id + "F6", {"entities" : qUnion([Q0]), "transformType" : TransformType.TRANSLATION_3D, "dx" : 0 * mm, "dy" : 0 * mm, "dz" : 15 * mm, "makeCopy" : true});
        }
        {
            var Q0;
            Q0=makeQuery(id+"F6.opPattern","COPY",BODY,{"derivedFrom":makeQuery(id+"F3.opExtrude","SWEPT_BODY",BODY,{"disambiguationData":[OSD([sQuery(id+"F2.wireOp",EDGE,"E10.bottom"),sQuery(id+"F2.wireOp",EDGE,"E10.top"),sQuery(id+"F2.wireOp",EDGE,"E10.left"),sQuery(id+"F2.wireOp",EDGE,"E10.right"),sQuery(id+"F2.wireOp",EDGE,"E12"),sQuery(id+"F2.wireOp",EDGE,"E13"),sQuery(id+"F2.wireOp",EDGE,"E14"),sQuery(id+"F2.wireOp",EDGE,"E16"),sQuery(id+"F2.wireOp",EDGE,"E17"),sQuery(id+"F2.wireOp",EDGE,"E18"),sQuery(id+"F2.wireOp",EDGE,"E19")])]}),"instanceName":"1"});
            deleteBodies(context, id + "F7", {"entities" : qUnion([Q0])});
        }
        {
            var Q0;
            Q0=makeQuery(id+"F3.opExtrude","SWEPT_BODY",BODY,{"disambiguationData":[OSD([sQuery(id+"F2.wireOp",EDGE,"E10.bottom"),sQuery(id+"F2.wireOp",EDGE,"E10.top"),sQuery(id+"F2.wireOp",EDGE,"E10.left"),sQuery(id+"F2.wireOp",EDGE,"E10.right"),sQuery(id+"F2.wireOp",EDGE,"E12"),sQuery(id+"F2.wireOp",EDGE,"E13"),sQuery(id+"F2.wireOp",EDGE,"E14"),sQuery(id+"F2.wireOp",EDGE,"E16"),sQuery(id+"F2.wireOp",EDGE,"E17"),sQuery(id+"F2.wireOp",EDGE,"E18"),sQuery(id+"F2.wireOp",EDGE,"E19")])]});
            var Q1;
            Q1=qCreatedBy(makeId("Top.planeOp"),FACE);
            mirror(context, id + "F8", {"entities" : qUnion([Q0]), "mirrorPlane" : qUnion([Q1])});
        }
        {
            var Q0;
            Q0=sQuery(id+"F1.wireOp",VERTEX,"E8.direction2.end");
            var Q1;
            Q1=qCreatedBy(makeId("Right.planeOp"),FACE);
            cPlane(context, id + "F9", {"entities" : qUnion([Q0, Q1]), "cplaneType" : CPlaneType.PLANE_POINT, "offset" : 25 * mm, "width" : 150 * mm, "height" : 150 * mm});
        }
        {
            var Q0;
            Q0=qCreatedBy(id+"F9.planeOp",FACE);
            var sketch = newSketch(context, id + "F10", { "sketchPlane" : qUnion([Q0])});
            skPoint(sketch, "E25.0", {"position": v(35, 0) * mm});
            skLineSegment(sketch, "E26", {"start": v(35, 0) * mm, "end": v(35, 430) * mm, "construction": true});
            skLineSegment(sketch, "E27", {"start": v(35, 273.15) * mm, "end": v(-238.15, 0) * mm});
            skLineSegment(sketch, "E28", {"start": v(35, 358) * mm, "end": v(-323, 0) * mm});
            skLineSegment(sketch, "E29", {"start": v(-535, 0) * mm, "end": v(-535, 430) * mm, "construction": true});
            skLineSegment(sketch, "E30", {"start": v(35, 358) * mm, "end": v(35, 273.15) * mm});
            skLineSegment(sketch, "E31", {"start": v(-238.15, 0) * mm, "end": v(-323, 0) * mm});
            skPoint(sketch, "E32", {"position": v(-300.23, 0) * mm});
            skLineSegment(sketch, "E33", {"start": v(-535, 430) * mm, "end": v(35, 430) * mm, "construction": true});
            skSolve(sketch);
        }
        {
            var Q0;
            Q0=makeQuery(id+"F10.imprint","IMPRINT",FACE,{"disambiguationData":[TD([[makeQuery(id+"F10.imprint","IMPRINT",EDGE,{"derivedFrom":sQuery(id+"F10.wireOp",EDGE,"E27")}),-1.0]])]});
            extrude(context, id + "F11", {"entities" : qUnion([Q0]), "endBound" : BoundingType.SYMMETRIC, "depth" : 30 * mm, "offsetDistance" : 25 * mm});
        }
        {
            var Q0;
            Q0=makeQuery(id+"F11.opExtrude","SWEPT_FACE",FACE,{"disambiguationData":[OSD([sQuery(id+"F10.wireOp",EDGE,"E31")])]});
            var sketch = newSketch(context, id + "F12", { "sketchPlane" : qUnion([Q0])});
            skLineSegment(sketch, "E34.0", {"start": v(60, 323) * mm, "end": v(30, 323) * mm, "construction": true});
            skLineSegment(sketch, "E35.0", {"start": v(45, 238.15) * mm, "end": v(45, 323) * mm, "construction": true});
            skCircle(sketch, "E36", {"center": v(45, 300.23) * mm, "radius": 3.25 * mm, "construction": true});
            skLineSegment(sketch, "E37.bottom", {"start": v(-10, 315) * mm, "end": v(90, 315) * mm});
            skLineSegment(sketch, "E37.top", {"start": v(-10, 285) * mm, "end": v(90, 285) * mm});
            skLineSegment(sketch, "E37.left", {"start": v(-10, 315) * mm, "end": v(-10, 285) * mm});
            skLineSegment(sketch, "E37.right", {"start": v(90, 315) * mm, "end": v(90, 285) * mm});
            skCircle(sketch, "E38", {"center": v(45, 300.23) * mm, "radius": 2.5 * mm});
            skPoint(sketch, "E39.0", {"position": v(0, 300) * mm});
            skPoint(sketch, "E39.1", {"position": v(75, 300) * mm});
            skCircle(sketch, "E40", {"center": v(0, 300) * mm, "radius": 3.25 * mm});
            skCircle(sketch, "E41", {"center": v(75, 300) * mm, "radius": 3.25 * mm});
            skSolve(sketch);
        }
        {
            var Q0;
            Q0 = qSketchRegion(id + "F12", true);
            extrude(context, id + "F13", {"entities" : qUnion([Q0]), "depth" : 10 * mm, "offsetDistance" : 25 * mm});
        }
        {
            var Q0;
            Q0=qCreatedBy(makeId("Right.planeOp"),FACE);
            var Q1;
            Q1=sQuery(id+"F0.wireOp",VERTEX,"E1.3.2.0.center");
            cPlane(context, id + "F14", {"entities" : qUnion([Q0, Q1]), "cplaneType" : CPlaneType.PLANE_POINT, "offset" : 25 * mm, "width" : 150 * mm, "height" : 150 * mm});
        }
        {
            var Q0;
            Q0=qCreatedBy(id+"F14.planeOp",FACE);
            var sketch = newSketch(context, id + "F15", { "sketchPlane" : qUnion([Q0])});
            skLineSegment(sketch, "E42.0", {"start": v(35, 0) * mm, "end": v(35, 430) * mm, "construction": true});
            skLineSegment(sketch, "E42.1", {"start": v(-535, 0) * mm, "end": v(-535, 430) * mm, "construction": true});
            skLineSegment(sketch, "E43", {"start": v(-535, 430) * mm, "end": v(35, 430) * mm, "construction": true});
            skLineSegment(sketch, "E44", {"start": v(-250, 430) * mm, "end": v(-250, 0) * mm, "construction": true});
            skLineSegment(sketch, "E45", {"start": v(-535, 358) * mm, "end": v(-535, 273.15) * mm});
            skLineSegment(sketch, "E46", {"start": v(-535, 273.15) * mm, "end": v(-261.85, 0) * mm});
            skLineSegment(sketch, "E47", {"start": v(-261.85, 0) * mm, "end": v(-177, 0) * mm});
            skLineSegment(sketch, "E48", {"start": v(-177, 0) * mm, "end": v(-535, 358) * mm});
            skPoint(sketch, "E49", {"position": v(-535, 375) * mm});
            skPoint(sketch, "E50", {"position": v(-199.77, 0) * mm});
            skSolve(sketch);
        }
        {
            var Q0;
            Q0=makeQuery(id+"F15.imprint","IMPRINT",FACE,{"disambiguationData":[TD([[makeQuery(id+"F15.imprint","IMPRINT",EDGE,{"derivedFrom":sQuery(id+"F15.wireOp",EDGE,"E45")}),1.0]])]});
            extrude(context, id + "F16", {"entities" : qUnion([Q0]), "endBound" : BoundingType.SYMMETRIC, "depth" : 30 * mm, "offsetDistance" : 25 * mm});
        }
        {
            var Q0;
            Q0=qCreatedBy(makeId("Front.planeOp"),FACE);
            var Q1;
            Q1=sQuery(id+"F1.wireOp",VERTEX,"E8.1.1.0.center");
            cPlane(context, id + "F17", {"entities" : qUnion([Q0, Q1]), "cplaneType" : CPlaneType.PLANE_POINT, "offset" : 25 * mm, "width" : 150 * mm, "height" : 150 * mm});
        }
        {
            var Q0;
            Q0=qCreatedBy(id+"F17.planeOp",FACE);
            var sketch = newSketch(context, id + "F18", { "sketchPlane" : qUnion([Q0])});
            skPoint(sketch, "E51.0", {"position": v(30, 0) * mm});
            skLineSegment(sketch, "E52", {"start": v(30, 0) * mm, "end": v(30, 430) * mm, "construction": true});
            skLineSegment(sketch, "E53", {"start": v(-730, 0) * mm, "end": v(-730, 430) * mm, "construction": true});
            skLineSegment(sketch, "E54", {"start": v(-350, 0) * mm, "end": v(-350, 430) * mm, "construction": true});
            skLineSegment(sketch, "E55", {"start": v(30, 353) * mm, "end": v(30, 268.15) * mm});
            skLineSegment(sketch, "E56", {"start": v(30, 268.15) * mm, "end": v(-238.15, 0) * mm});
            skLineSegment(sketch, "E57", {"start": v(-238.15, 0) * mm, "end": v(-323, 0) * mm});
            skLineSegment(sketch, "E58", {"start": v(-323, 0) * mm, "end": v(30, 353) * mm});
            skPoint(sketch, "E59", {"position": v(-300.23, 0) * mm});
            skSolve(sketch);
        }
        {
            var Q0;
            Q0=makeQuery(id+"F18.imprint","IMPRINT",FACE,{"disambiguationData":[TD([[makeQuery(id+"F18.imprint","IMPRINT",EDGE,{"derivedFrom":sQuery(id+"F18.wireOp",EDGE,"E55")}),-1.0]])]});
            extrude(context, id + "F19", {"entities" : qUnion([Q0]), "endBound" : BoundingType.SYMMETRIC, "depth" : 30 * mm, "offsetDistance" : 25 * mm});
        }
        {
            var Q0;
            Q0=sQuery(id+"F0.wireOp",VERTEX,"E4.0.14.2.center");
            var Q1;
            Q1=sQuery(id+"F0.wireOp",VERTEX,"E4.0.14.4.center");
            var Q2;
            Q2=sQuery(id+"F18.wireOp",VERTEX,"E54.end");
            cPlane(context, id + "F20", {"entities" : qUnion([Q0, Q1, Q2]), "cplaneType" : CPlaneType.THREE_POINT, "offset" : 25 * mm, "width" : 150 * mm, "height" : 150 * mm});
        }
        {
            var Q0;
            Q0=makeQuery(id+"F19.opExtrude","SWEPT_BODY",BODY,{"disambiguationData":[OSD([sQuery(id+"F18.wireOp",EDGE,"E55"),sQuery(id+"F18.wireOp",EDGE,"E56"),sQuery(id+"F18.wireOp",EDGE,"E57"),sQuery(id+"F18.wireOp",EDGE,"E58")])]});
            var Q1;
            Q1=qCreatedBy(id+"F20.planeOp",FACE);
            mirror(context, id + "F21", {"entities" : qUnion([Q0]), "mirrorPlane" : qUnion([Q1])});
        }
        {
            var Q0;
            Q0=makeQuery(id+"F16.opExtrude","SWEPT_BODY",BODY,{"disambiguationData":[OSD([sQuery(id+"F15.wireOp",EDGE,"E45"),sQuery(id+"F15.wireOp",EDGE,"E46"),sQuery(id+"F15.wireOp",EDGE,"E47"),sQuery(id+"F15.wireOp",EDGE,"E48")])]});
            var Q1;
            Q1=qCreatedBy(id+"F20.planeOp",FACE);
            mirror(context, id + "F22", {"entities" : qUnion([Q0]), "mirrorPlane" : qUnion([Q1])});
        }
        {
            var Q0;
            Q0=makeQuery(id+"F11.opExtrude","SWEPT_BODY",BODY,{"disambiguationData":[OSD([sQuery(id+"F10.wireOp",EDGE,"E27"),sQuery(id+"F10.wireOp",EDGE,"E28"),sQuery(id+"F10.wireOp",EDGE,"E30"),sQuery(id+"F10.wireOp",EDGE,"E31")])]});
            var Q1;
            Q1=qCreatedBy(id+"F20.planeOp",FACE);
            mirror(context, id + "F23", {"entities" : qUnion([Q0]), "mirrorPlane" : qUnion([Q1])});
        }
        {
            var Q0;
            Q0=makeQuery(id+"F1.imprint","IMPRINT",FACE,{"disambiguationData":[TD([[makeQuery(id+"F1.imprint","IMPRINT",EDGE,{"derivedFrom":sQuery(id+"F1.wireOp",EDGE,"E6.bottom")}),1.0]])]});
            extrude(context, id + "F24", {"entities" : qUnion([Q0]), "depth" : 430 * mm, "offsetDistance" : 25 * mm});
        }
        {
            var Q0;
            Q0=sQuery(id+"F15.wireOp",EDGE,"E43");
            cPoint(context, id + "F25", {"entities" : qUnion([Q0]), "parameter" : 0.5});
        }
        {
            var Q0;
            Q0 = qCreatedBy(id + "F25" ,VERTEX);
            var Q1;
            Q1=sQuery(id+"F0.wireOp",VERTEX,"E2.3.10.0.center");
            var Q2;
            Q2=sQuery(id+"F0.wireOp",VERTEX,"E2.4.10.0.center");
            cPlane(context, id + "F26", {"entities" : qUnion([Q0, Q1, Q2]), "cplaneType" : CPlaneType.THREE_POINT, "offset" : 25 * mm, "width" : 150 * mm, "height" : 150 * mm});
        }
        {
            var Q0;
            Q0=makeQuery(id+"F24.opExtrude","SWEPT_BODY",BODY,{"disambiguationData":[OSD([sQuery(id+"F1.wireOp",EDGE,"E6.bottom"),sQuery(id+"F1.wireOp",EDGE,"E6.top"),sQuery(id+"F1.wireOp",EDGE,"E6.left"),sQuery(id+"F1.wireOp",EDGE,"E6.right"),sQuery(id+"F1.wireOp",EDGE,"E7"),sQuery(id+"F1.wireOp",EDGE,"E8.0.1.0"),sQuery(id+"F1.wireOp",EDGE,"E8.1.0.0"),sQuery(id+"F1.wireOp",EDGE,"E8.1.1.0")])]});
            var Q1;
            Q1=qCreatedBy(id+"F26.planeOp",FACE);
            mirror(context, id + "F27", {"entities" : qUnion([Q0]), "mirrorPlane" : qUnion([Q1])});
        }
        {
            var Q0;
            Q0=makeQuery(id+"F24.opExtrude","SWEPT_BODY",BODY,{"disambiguationData":[OSD([sQuery(id+"F1.wireOp",EDGE,"E6.bottom"),sQuery(id+"F1.wireOp",EDGE,"E6.top"),sQuery(id+"F1.wireOp",EDGE,"E6.left"),sQuery(id+"F1.wireOp",EDGE,"E6.right"),sQuery(id+"F1.wireOp",EDGE,"E7"),sQuery(id+"F1.wireOp",EDGE,"E8.0.1.0"),sQuery(id+"F1.wireOp",EDGE,"E8.1.0.0"),sQuery(id+"F1.wireOp",EDGE,"E8.1.1.0")])]});
            var Q1;
            Q1=qCreatedBy(id+"F20.planeOp",FACE);
            mirror(context, id + "F28", {"entities" : qUnion([Q0]), "mirrorPlane" : qUnion([Q1])});
        }
        {
            var Q0;
            Q0=makeQuery(id+"F28.opPattern","COPY",BODY,{"derivedFrom":makeQuery(id+"F24.opExtrude","SWEPT_BODY",BODY,{"disambiguationData":[OSD([sQuery(id+"F1.wireOp",EDGE,"E6.bottom"),sQuery(id+"F1.wireOp",EDGE,"E6.top"),sQuery(id+"F1.wireOp",EDGE,"E6.left"),sQuery(id+"F1.wireOp",EDGE,"E6.right"),sQuery(id+"F1.wireOp",EDGE,"E7"),sQuery(id+"F1.wireOp",EDGE,"E8.0.1.0"),sQuery(id+"F1.wireOp",EDGE,"E8.1.0.0"),sQuery(id+"F1.wireOp",EDGE,"E8.1.1.0")])]}),"instanceName":"1"});
            var Q1;
            Q1=qCreatedBy(id+"F26.planeOp",FACE);
            mirror(context, id + "F29", {"entities" : qUnion([Q0]), "mirrorPlane" : qUnion([Q1])});
        }
    });
